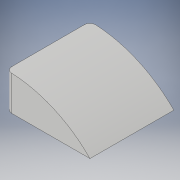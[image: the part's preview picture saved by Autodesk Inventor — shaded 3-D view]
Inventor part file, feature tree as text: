
AUTODESK INVENTOR PART (.ipt)
format: ipt  version: 2019.4 (Build 234330000, 330)  size: 98,816 bytes
history: native  units: mm
features: extrude x1, fillet x1, sketch x1
ambient origin geometry x8: Origin, YZ Plane, XZ Plane, XY Plane, X Axis, Y Axis, Z Axis, Center Point
bodies: Solid1 (feature_tree)
feature tree (3):
  extrude  "Extrusion1"  Depth=2.0mm
  fillet  "Fillet1"  Radius=30.0mm
  sketch  "Sketch1"  dims[d0=30.0mm d1=12.5mm d2=30.0mm d3=0.0mm d4=2.0mm]
